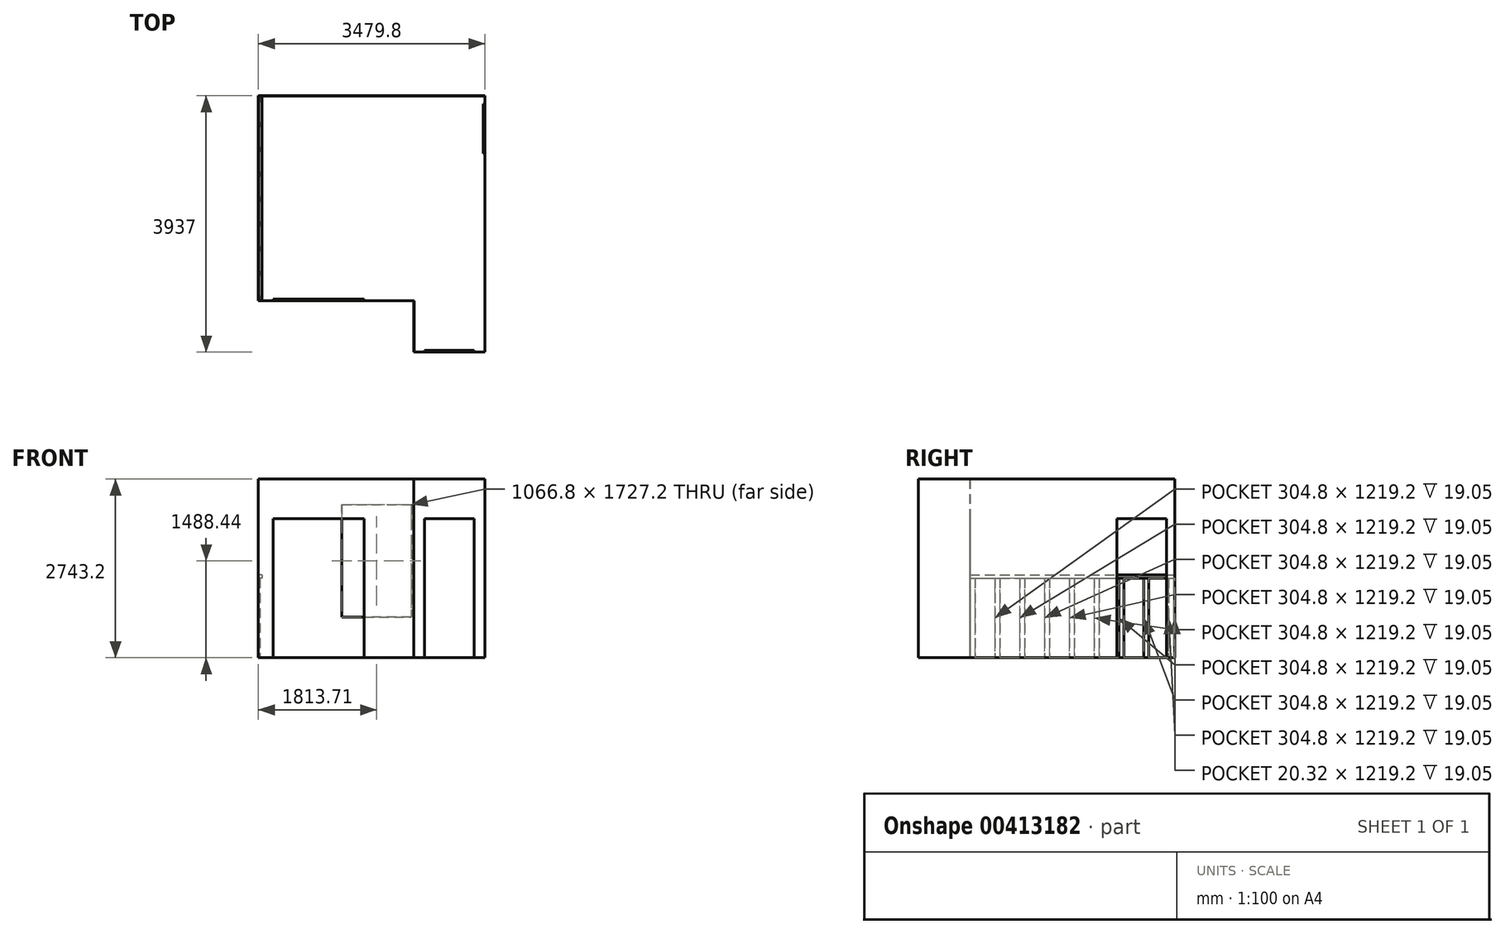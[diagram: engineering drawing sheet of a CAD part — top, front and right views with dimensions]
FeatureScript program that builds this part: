
annotation { "Feature Type Name" : "Feature", "Feature Type Description" : "" }
export const myFeature = defineFeature(function(context is Context, id is Id, definition is map)
    precondition{}
    {
        {
            var Q0;
            Q0=qCreatedBy(makeId("Top.planeOp"),FACE);
            var sketch = newSketch(context, id + "F0", { "sketchPlane" : qUnion([Q0])});
            skLineSegment(sketch, "E0", {"start": v(0, 0) * mm, "end": v(0, 3149.6) * mm});
            skLineSegment(sketch, "E1", {"start": v(0, 3149.6) * mm, "end": v(3479.8, 3149.6) * mm});
            skLineSegment(sketch, "E2", {"start": v(3479.8, 3149.6) * mm, "end": v(3479.8, -787.4) * mm});
            skLineSegment(sketch, "E3", {"start": v(3479.8, -787.4) * mm, "end": v(2387.6, -787.4) * mm});
            skLineSegment(sketch, "E4", {"start": v(2387.6, -787.4) * mm, "end": v(2387.6, 0) * mm});
            skLineSegment(sketch, "E5", {"start": v(2387.6, 0) * mm, "end": v(0, 0) * mm});
            skSolve(sketch);
        }
        {
            var Q0;
            Q0 = qSketchRegion(id + "F0", true);
            extrude(context, id + "F1", {"entities" : qUnion([Q0]), "depth" : 2743.2 * mm});
        }
        {
            var Q0;
            Q0=makeQuery(id+"F1.opExtrude","CAP_FACE",FACE,{"disambiguationData":[OSD([sQuery(id+"F0.wireOp",EDGE,"E0"),sQuery(id+"F0.wireOp",EDGE,"E1"),sQuery(id+"F0.wireOp",EDGE,"E2"),sQuery(id+"F0.wireOp",EDGE,"E3"),sQuery(id+"F0.wireOp",EDGE,"E4"),sQuery(id+"F0.wireOp",EDGE,"E5")])],"isStart":false});
            shell(context, id + "F2", {"entities" : qUnion([Q0]), "thickness" : 2.54 * mm});
        }
        {
            var Q0;
            Q0=makeQuery(id+"F1.opExtrude","SWEPT_FACE",FACE,{"disambiguationData":[OSD([sQuery(id+"F0.wireOp",EDGE,"E3")])]});
            var sketch = newSketch(context, id + "F3", { "sketchPlane" : qUnion([Q0])});
            skLineSegment(sketch, "E6.bottom", {"start": v(2552.7, 2133.6) * mm, "end": v(3314.7, 2133.6) * mm});
            skLineSegment(sketch, "E6.top", {"start": v(2552.7, 0) * mm, "end": v(3314.7, 0) * mm});
            skLineSegment(sketch, "E6.left", {"start": v(2552.7, 2133.6) * mm, "end": v(2552.7, 0) * mm});
            skLineSegment(sketch, "E6.right", {"start": v(3314.7, 2133.6) * mm, "end": v(3314.7, 0) * mm});
            skLineSegment(sketch, "E7", {"start": v(2552.7, 0) * mm, "end": v(2387.6, 0) * mm, "construction": true});
            skLineSegment(sketch, "E8", {"start": v(3314.7, 0) * mm, "end": v(3479.8, 0) * mm, "construction": true});
            skSolve(sketch);
        }
        {
            var Q0;
            Q0 = qSketchRegion(id + "F3", true);
            extrude(context, id + "F4", {"entities" : qUnion([Q0]), "operationType" : NewBodyOperationType.REMOVE, "oppositeDirection" : true, "depth" : 25.4 * mm});
        }
        {
            var Q0;
            Q0=makeQuery(id+"F1.opExtrude","SWEPT_FACE",FACE,{"disambiguationData":[OSD([sQuery(id+"F0.wireOp",EDGE,"E5")])]});
            var sketch = newSketch(context, id + "F5", { "sketchPlane" : qUnion([Q0])});
            skLineSegment(sketch, "E9.bottom", {"start": v(228.6, 2133.6) * mm, "end": v(1625.6, 2133.6) * mm});
            skLineSegment(sketch, "E9.top", {"start": v(228.6, 0) * mm, "end": v(1625.6, 0) * mm});
            skLineSegment(sketch, "E9.left", {"start": v(228.6, 2133.6) * mm, "end": v(228.6, 0) * mm});
            skLineSegment(sketch, "E9.right", {"start": v(1625.6, 2133.6) * mm, "end": v(1625.6, 0) * mm});
            skLineSegment(sketch, "E10", {"start": v(228.6, 0) * mm, "end": v(0, 0) * mm, "construction": true});
            skSolve(sketch);
        }
        {
            var Q0;
            Q0=makeQuery(id+"F5.imprint","IMPRINT",FACE,{"disambiguationData":[TD([[makeQuery(id+"F5.imprint","IMPRINT",EDGE,{"derivedFrom":sQuery(id+"F5.wireOp",EDGE,"E9.bottom")}),-1.0]])]});
            extrude(context, id + "F6", {"entities" : qUnion([Q0]), "operationType" : NewBodyOperationType.REMOVE, "oppositeDirection" : true, "depth" : 25.4 * mm});
        }
        {
            var Q0;
            Q0=makeQuery(id+"F1.opExtrude","SWEPT_FACE",FACE,{"disambiguationData":[OSD([sQuery(id+"F0.wireOp",EDGE,"E2")])]});
            var sketch = newSketch(context, id + "F7", { "sketchPlane" : qUnion([Q0])});
            skLineSegment(sketch, "E11.bottom", {"start": v(2260.6, 2133.6) * mm, "end": v(3022.6, 2133.6) * mm});
            skLineSegment(sketch, "E11.top", {"start": v(2260.6, 0) * mm, "end": v(3022.6, 0) * mm});
            skLineSegment(sketch, "E11.left", {"start": v(2260.6, 2133.6) * mm, "end": v(2260.6, 0) * mm});
            skLineSegment(sketch, "E11.right", {"start": v(3022.6, 2133.6) * mm, "end": v(3022.6, 0) * mm});
            skSolve(sketch);
        }
        {
            var Q0;
            Q0 = qSketchRegion(id + "F7", true);
            extrude(context, id + "F8", {"entities" : qUnion([Q0]), "operationType" : NewBodyOperationType.REMOVE, "oppositeDirection" : true, "depth" : 25.4 * mm});
        }
        {
            var Q0;
            Q0=makeQuery(id+"F2.opShell","OFFSET_FACE",FACE,{"disambiguationData":[OSD([sQuery(id+"F0.wireOp",EDGE,"E1")])]});
            var sketch = newSketch(context, id + "F9", { "sketchPlane" : qUnion([Q0])});
            skLineSegment(sketch, "E12.bottom", {"start": v(1280.3, 2352.04) * mm, "end": v(2347.1, 2352.04) * mm});
            skLineSegment(sketch, "E12.top", {"start": v(1280.3, 624.84) * mm, "end": v(2347.1, 624.84) * mm});
            skLineSegment(sketch, "E12.left", {"start": v(1280.3, 2352.04) * mm, "end": v(1280.3, 624.84) * mm});
            skLineSegment(sketch, "E12.right", {"start": v(2347.1, 2352.04) * mm, "end": v(2347.1, 624.84) * mm});
            skSolve(sketch);
        }
        {
            var Q0;
            Q0=makeQuery(id+"F9.imprint","IMPRINT",FACE,{"disambiguationData":[TD([[makeQuery(id+"F9.imprint","IMPRINT",EDGE,{"derivedFrom":sQuery(id+"F9.wireOp",EDGE,"E12.bottom")}),-1.0]])]});
            extrude(context, id + "F10", {"entities" : qUnion([Q0]), "operationType" : NewBodyOperationType.REMOVE, "oppositeDirection" : true, "depth" : 25.4 * mm});
        }
        {
            var Q0;
            Q0=makeQuery(id+"F2.opShell","OFFSET_FACE",FACE,{"disambiguationData":[OSD([sQuery(id+"F0.wireOp",EDGE,"E0"),sQuery(id+"F0.wireOp",EDGE,"E1"),sQuery(id+"F0.wireOp",EDGE,"E2"),sQuery(id+"F0.wireOp",EDGE,"E3"),sQuery(id+"F0.wireOp",EDGE,"E4"),sQuery(id+"F0.wireOp",EDGE,"E5")])]});
            var sketch = newSketch(context, id + "F11", { "sketchPlane" : qUnion([Q0])});
            skLineSegment(sketch, "E13.bottom", {"start": v(2.54, 2.54) * mm, "end": v(21.59, 2.54) * mm});
            skLineSegment(sketch, "E13.top", {"start": v(2.54, 78.74) * mm, "end": v(21.59, 78.74) * mm});
            skLineSegment(sketch, "E13.left", {"start": v(2.54, 2.54) * mm, "end": v(2.54, 78.74) * mm});
            skLineSegment(sketch, "E13.right", {"start": v(21.59, 2.54) * mm, "end": v(21.59, 78.74) * mm});
            skLineSegment(sketch, "E14", {"start": v(21.59, 78.74) * mm, "end": v(21.59, 383.54) * mm, "construction": true});
            skLineSegment(sketch, "E15.0.1.0", {"start": v(21.59, 459.74) * mm, "end": v(21.59, 764.54) * mm, "construction": true});
            skLineSegment(sketch, "E15.0.1.1", {"start": v(21.59, 383.54) * mm, "end": v(21.59, 459.74) * mm});
            skLineSegment(sketch, "E15.0.1.2", {"start": v(2.54, 383.54) * mm, "end": v(2.54, 459.74) * mm});
            skLineSegment(sketch, "E15.0.1.3", {"start": v(2.54, 383.54) * mm, "end": v(21.59, 383.54) * mm});
            skLineSegment(sketch, "E15.0.1.4", {"start": v(2.54, 459.74) * mm, "end": v(21.59, 459.74) * mm});
            skLineSegment(sketch, "E15.0.2.0", {"start": v(21.59, 840.74) * mm, "end": v(21.59, 1145.54) * mm, "construction": true});
            skLineSegment(sketch, "E15.0.2.1", {"start": v(21.59, 764.54) * mm, "end": v(21.59, 840.74) * mm});
            skLineSegment(sketch, "E15.0.2.2", {"start": v(2.54, 764.54) * mm, "end": v(2.54, 840.74) * mm});
            skLineSegment(sketch, "E15.0.2.3", {"start": v(2.54, 764.54) * mm, "end": v(21.59, 764.54) * mm});
            skLineSegment(sketch, "E15.0.2.4", {"start": v(2.54, 840.74) * mm, "end": v(21.59, 840.74) * mm});
            skLineSegment(sketch, "E15.0.3.0", {"start": v(21.59, 1221.74) * mm, "end": v(21.59, 1526.54) * mm, "construction": true});
            skLineSegment(sketch, "E15.0.3.1", {"start": v(21.59, 1145.54) * mm, "end": v(21.59, 1221.74) * mm});
            skLineSegment(sketch, "E15.0.3.2", {"start": v(2.54, 1145.54) * mm, "end": v(2.54, 1221.74) * mm});
            skLineSegment(sketch, "E15.0.3.3", {"start": v(2.54, 1145.54) * mm, "end": v(21.59, 1145.54) * mm});
            skLineSegment(sketch, "E15.0.3.4", {"start": v(2.54, 1221.74) * mm, "end": v(21.59, 1221.74) * mm});
            skLineSegment(sketch, "E15.0.4.0", {"start": v(21.59, 1602.74) * mm, "end": v(21.59, 1907.54) * mm, "construction": true});
            skLineSegment(sketch, "E15.0.4.1", {"start": v(21.59, 1526.54) * mm, "end": v(21.59, 1602.74) * mm});
            skLineSegment(sketch, "E15.0.4.2", {"start": v(2.54, 1526.54) * mm, "end": v(2.54, 1602.74) * mm});
            skLineSegment(sketch, "E15.0.4.3", {"start": v(2.54, 1526.54) * mm, "end": v(21.59, 1526.54) * mm});
            skLineSegment(sketch, "E15.0.4.4", {"start": v(2.54, 1602.74) * mm, "end": v(21.59, 1602.74) * mm});
            skLineSegment(sketch, "E15.0.5.0", {"start": v(21.59, 1983.74) * mm, "end": v(21.59, 2288.54) * mm, "construction": true});
            skLineSegment(sketch, "E15.0.5.1", {"start": v(21.59, 1907.54) * mm, "end": v(21.59, 1983.74) * mm});
            skLineSegment(sketch, "E15.0.5.2", {"start": v(2.54, 1907.54) * mm, "end": v(2.54, 1983.74) * mm});
            skLineSegment(sketch, "E15.0.5.3", {"start": v(2.54, 1907.54) * mm, "end": v(21.59, 1907.54) * mm});
            skLineSegment(sketch, "E15.0.5.4", {"start": v(2.54, 1983.74) * mm, "end": v(21.59, 1983.74) * mm});
            skLineSegment(sketch, "E15.direction1", {"start": v(2.54, 2.54) * mm, "end": v(143.76, 2.54) * mm, "construction": true});
            skLineSegment(sketch, "E15.direction2", {"start": v(2.54, 2.54) * mm, "end": v(2.54, 383.54) * mm, "construction": true});
            skLineSegment(sketch, "E16.0.0.6", {"start": v(21.59, 2364.74) * mm, "end": v(21.59, 2669.54) * mm, "construction": true});
            skLineSegment(sketch, "E16.3.0.6", {"start": v(21.59, 2288.54) * mm, "end": v(21.59, 2364.74) * mm});
            skLineSegment(sketch, "E16.6.0.6", {"start": v(2.54, 2288.54) * mm, "end": v(2.54, 2364.74) * mm});
            skLineSegment(sketch, "E16.9.0.6", {"start": v(2.54, 2288.54) * mm, "end": v(21.59, 2288.54) * mm});
            skLineSegment(sketch, "E16.12.0.6", {"start": v(2.54, 2364.74) * mm, "end": v(21.59, 2364.74) * mm});
            skLineSegment(sketch, "E17.0.0.7", {"start": v(21.59, 2745.74) * mm, "end": v(21.59, 3050.54) * mm, "construction": true});
            skLineSegment(sketch, "E17.3.0.7", {"start": v(21.59, 2669.54) * mm, "end": v(21.59, 2745.74) * mm});
            skLineSegment(sketch, "E17.6.0.7", {"start": v(2.54, 2669.54) * mm, "end": v(2.54, 2745.74) * mm});
            skLineSegment(sketch, "E17.9.0.7", {"start": v(2.54, 2669.54) * mm, "end": v(21.59, 2669.54) * mm});
            skLineSegment(sketch, "E17.12.0.7", {"start": v(2.54, 2745.74) * mm, "end": v(21.59, 2745.74) * mm});
            skLineSegment(sketch, "E18.bottom", {"start": v(21.59, 3050.54) * mm, "end": v(2.54, 3050.54) * mm});
            skLineSegment(sketch, "E18.top", {"start": v(21.59, 3126.74) * mm, "end": v(2.54, 3126.74) * mm});
            skLineSegment(sketch, "E18.left", {"start": v(21.59, 3050.54) * mm, "end": v(21.59, 3126.74) * mm});
            skLineSegment(sketch, "E18.right", {"start": v(2.54, 3050.54) * mm, "end": v(2.54, 3126.74) * mm});
            skSolve(sketch);
        }
        {
            var Q0;
            Q0 = qSketchRegion(id + "F11", true);
            extrude(context, id + "F12", {"entities" : qUnion([Q0]), "operationType" : NewBodyOperationType.ADD, "depth" : 1219.2 * mm});
        }
        {
            var Q0;
            Q0=makeQuery(id+"F2.opShell","OFFSET_FACE",FACE,{"disambiguationData":[OSD([sQuery(id+"F0.wireOp",EDGE,"E0")])]});
            var sketch = newSketch(context, id + "F13", { "sketchPlane" : qUnion([Q0])});
            skLineSegment(sketch, "E19.bottom", {"start": v(2.54, 1221.74) * mm, "end": v(3147.06, 1221.74) * mm});
            skLineSegment(sketch, "E19.top", {"start": v(2.54, 1272.54) * mm, "end": v(3147.06, 1272.54) * mm});
            skLineSegment(sketch, "E19.left", {"start": v(2.54, 1221.74) * mm, "end": v(2.54, 1272.54) * mm});
            skLineSegment(sketch, "E19.right", {"start": v(3147.06, 1221.74) * mm, "end": v(3147.06, 1272.54) * mm});
            skSolve(sketch);
        }
        {
            var Q0;
            Q0=makeQuery(id+"F13.imprint","IMPRINT",FACE,{"disambiguationData":[TD([[makeQuery(id+"F13.imprint","IMPRINT",EDGE,{"derivedFrom":sQuery(id+"F13.wireOp",EDGE,"E19.top")}),-1.0]])]});
            extrude(context, id + "F14", {"entities" : qUnion([Q0]), "operationType" : NewBodyOperationType.ADD, "depth" : 50.8 * mm});
        }
    });
